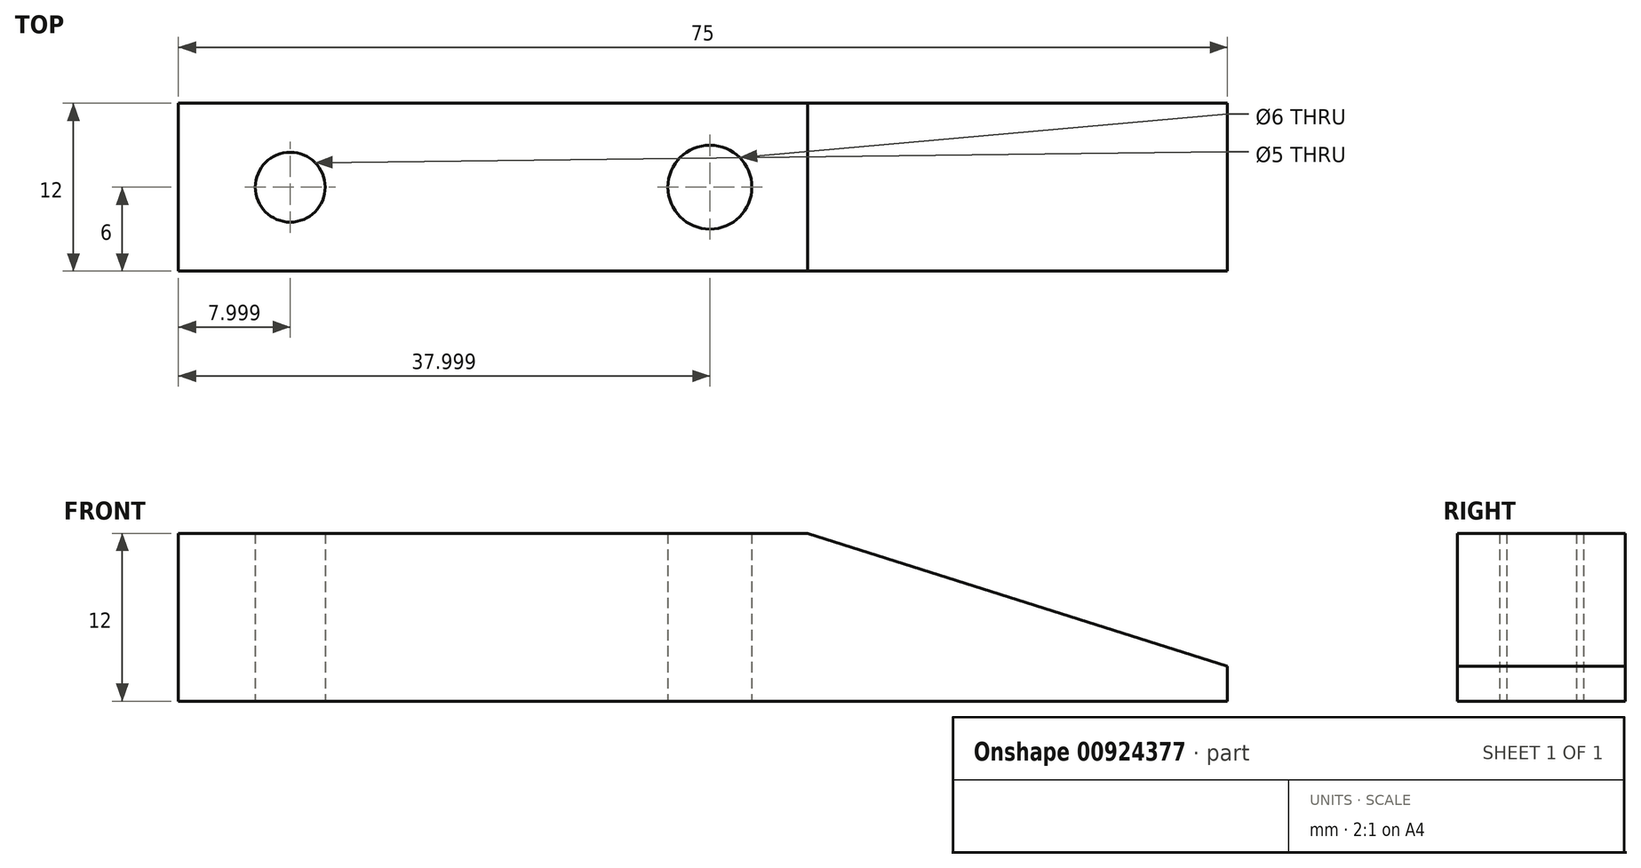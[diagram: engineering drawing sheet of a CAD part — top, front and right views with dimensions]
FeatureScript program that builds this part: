
annotation { "Feature Type Name" : "Feature", "Feature Type Description" : "" }
export const myFeature = defineFeature(function(context is Context, id is Id, definition is map)
    precondition{}
    {
        {
            var Q0;
            Q0=qCreatedBy(makeId("Front.planeOp"),FACE);
            var sketch = newSketch(context, id + "F0", { "sketchPlane" : qUnion([Q0])});
            skLineSegment(sketch, "E0", {"start": v(-36.35, 32.64) * mm, "end": v(8.65, 32.64) * mm});
            skLineSegment(sketch, "E1", {"start": v(8.65, 32.64) * mm, "end": v(38.65, 23.14) * mm});
            skLineSegment(sketch, "E2", {"start": v(38.65, 23.14) * mm, "end": v(38.65, 20.64) * mm});
            skLineSegment(sketch, "E3", {"start": v(38.65, 20.64) * mm, "end": v(-36.35, 20.64) * mm});
            skLineSegment(sketch, "E4", {"start": v(-36.35, 20.64) * mm, "end": v(-36.35, 32.64) * mm});
            skSolve(sketch);
        }
        {
            var Q0;
            Q0 = qSketchRegion(id + "F0", true);
            extrude(context, id + "F1", {"entities" : qUnion([Q0]), "depth" : 12 * mm, "offsetDistance" : 25 * mm});
        }
        {
            var Q0;
            Q0=makeQuery(id+"F1.opExtrude","SWEPT_FACE",FACE,{"disambiguationData":[OSD([sQuery(id+"F0.wireOp",EDGE,"E3")])]});
            var sketch = newSketch(context, id + "F2", { "sketchPlane" : qUnion([Q0])});
            skCircle(sketch, "E5", {"center": v(1.65, 6) * mm, "radius": 3 * mm});
            skSolve(sketch);
        }
        {
            var Q0;
            Q0 = qSketchRegion(id + "F2", true);
            extrude(context, id + "F3", {"entities" : qUnion([Q0]), "operationType" : NewBodyOperationType.REMOVE, "oppositeDirection" : true, "depth" : 25 * mm, "offsetDistance" : 25 * mm});
        }
        {
            var Q0;
            Q0=makeQuery(id+"F1.opExtrude","SWEPT_FACE",FACE,{"disambiguationData":[OSD([sQuery(id+"F0.wireOp",EDGE,"E3")])]});
            var sketch = newSketch(context, id + "F4", { "sketchPlane" : qUnion([Q0])});
            skCircle(sketch, "E6", {"center": v(-28.35, 6) * mm, "radius": 2.5 * mm});
            skSolve(sketch);
        }
        {
            var Q0;
            Q0 = qSketchRegion(id + "F4", true);
            extrude(context, id + "F5", {"entities" : qUnion([Q0]), "operationType" : NewBodyOperationType.REMOVE, "oppositeDirection" : true, "depth" : 25 * mm, "offsetDistance" : 25 * mm});
        }
    });
